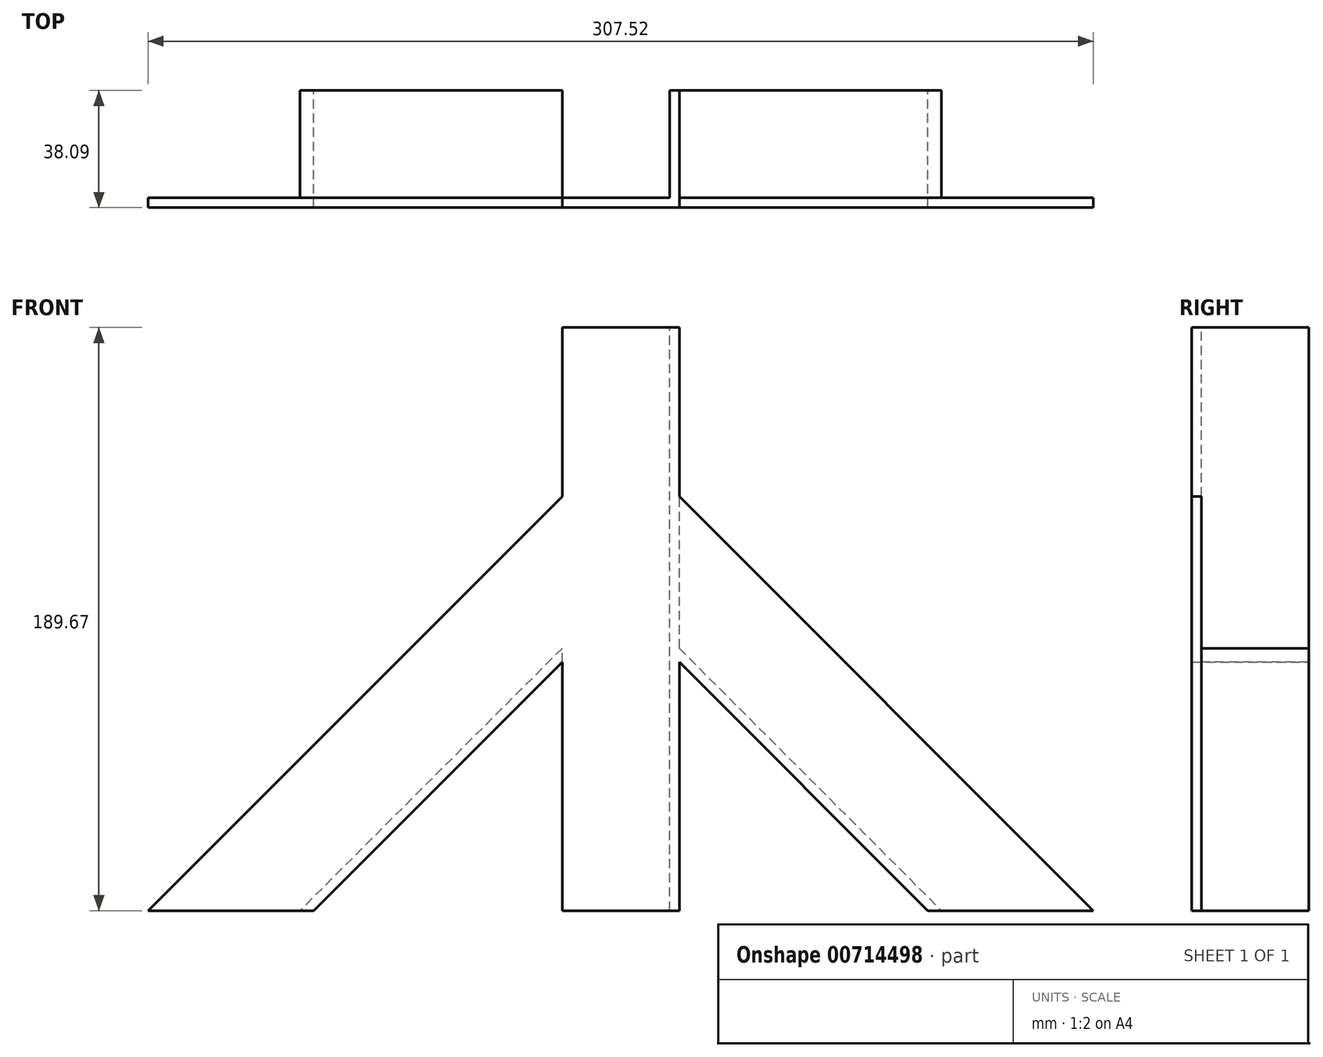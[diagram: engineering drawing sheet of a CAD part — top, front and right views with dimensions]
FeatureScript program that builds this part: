
annotation { "Feature Type Name" : "Feature", "Feature Type Description" : "" }
export const myFeature = defineFeature(function(context is Context, id is Id, definition is map)
    precondition{}
    {
        {
            var Q0;
            Q0=qCreatedBy(makeId("Front.planeOp"),FACE);
            var sketch = newSketch(context, id + "F0", { "sketchPlane" : qUnion([Q0])});
            skLineSegment(sketch, "E0.bottom", {"start": v(0, 0) * mm, "end": v(38.1, 0) * mm});
            skLineSegment(sketch, "E0.top", {"start": v(0, 189.67) * mm, "end": v(38.1, 189.67) * mm});
            skLineSegment(sketch, "E0.left", {"start": v(0, 0) * mm, "end": v(0, 189.67) * mm});
            skLineSegment(sketch, "E0.right", {"start": v(38.1, 0) * mm, "end": v(38.1, 189.67) * mm});
            skLineSegment(sketch, "E1", {"start": v(-80.83, 0) * mm, "end": v(0, 80.83) * mm});
            skLineSegment(sketch, "E2", {"start": v(-134.7, 0) * mm, "end": v(0, 134.7) * mm});
            skLineSegment(sketch, "E3", {"start": v(38.1, 134.7) * mm, "end": v(172.8, 0) * mm});
            skLineSegment(sketch, "E4", {"start": v(118.93, 0) * mm, "end": v(38.1, 80.83) * mm});
            skLineSegment(sketch, "E5", {"start": v(-134.7, 0) * mm, "end": v(-80.83, 0) * mm});
            skLineSegment(sketch, "E6", {"start": v(118.93, 0) * mm, "end": v(172.8, 0) * mm});
            skSolve(sketch);
        }
        {
            var Q0;
            {var subQ3=sQuery(id+"F0.wireOp",EDGE,"E0.bottom");Q0=makeQuery(id+"F0.imprint","IMPRINT",FACE,{"disambiguationData":[TD([[makeQuery(id+"F0.imprint","IMPRINT",EDGE,{"derivedFrom":subQ3}),1.0]])]});}
            var Q1;
            {var subQ0=sQuery(id+"F0.wireOp",EDGE,"E1");Q1=makeQuery(id+"F0.imprint","IMPRINT",FACE,{"disambiguationData":[TD([[makeQuery(id+"F0.imprint","IMPRINT",EDGE,{"derivedFrom":subQ0}),1.0]])]});}
            var Q2;
            {var subQ0=sQuery(id+"F0.wireOp",EDGE,"E3");Q2=makeQuery(id+"F0.imprint","IMPRINT",FACE,{"disambiguationData":[TD([[makeQuery(id+"F0.imprint","IMPRINT",EDGE,{"derivedFrom":subQ0}),-1.0]])]});}
            extrude(context, id + "F1", {"entities" : qUnion([Q0, Q1, Q2]), "depth" : 3.17 * mm, "offsetDistance" : 25.4 * mm});
        }
        {
            var Q0;
            Q0=makeQuery(id+"F1.opExtrude","CAP_FACE",FACE,{"disambiguationData":[OSD([sQuery(id+"F0.wireOp",EDGE,"E0.bottom"),sQuery(id+"F0.wireOp",EDGE,"E0.top"),sQuery(id+"F0.wireOp",EDGE,"E0.left"),sQuery(id+"F0.wireOp",EDGE,"E0.right"),sQuery(id+"F0.wireOp",EDGE,"E1"),sQuery(id+"F0.wireOp",EDGE,"E2"),sQuery(id+"F0.wireOp",EDGE,"E3"),sQuery(id+"F0.wireOp",EDGE,"E4"),sQuery(id+"F0.wireOp",EDGE,"E5"),sQuery(id+"F0.wireOp",EDGE,"E6")])],"isStart":true});
            var sketch = newSketch(context, id + "F2", { "sketchPlane" : qUnion([Q0])});
            skLineSegment(sketch, "E7.bottom", {"start": v(-38.1, 0) * mm, "end": v(-34.92, 0) * mm});
            skLineSegment(sketch, "E7.top", {"start": v(-38.1, 189.67) * mm, "end": v(-34.93, 189.67) * mm});
            skLineSegment(sketch, "E7.left", {"start": v(-38.1, 0) * mm, "end": v(-38.1, 189.67) * mm});
            skLineSegment(sketch, "E7.right", {"start": v(-34.92, 0) * mm, "end": v(-34.93, 189.67) * mm});
            skSolve(sketch);
        }
        {
            var Q0;
            {var subQ3=sQuery(id+"F2.wireOp",EDGE,"E7.bottom");Q0=makeQuery(id+"F2.imprint","IMPRINT",FACE,{"disambiguationData":[TD([[makeQuery(id+"F2.imprint","IMPRINT",EDGE,{"derivedFrom":subQ3}),-1.0]])]});}
            extrude(context, id + "F3", {"entities" : qUnion([Q0]), "operationType" : NewBodyOperationType.ADD, "depth" : 34.92 * mm, "offsetDistance" : 25.4 * mm});
        }
        {
            var Q0;
            {var subQ0=sQuery(id+"F0.wireOp",EDGE,"E3");var subQ1=sQuery(id+"F0.wireOp",EDGE,"E0.right");var subQ2=sQuery(id+"F0.wireOp",EDGE,"E0.top");var subQ3=sQuery(id+"F0.wireOp",EDGE,"E4");var subQ4=sQuery(id+"F0.wireOp",EDGE,"E0.bottom");var subQ5=sQuery(id+"F0.wireOp",EDGE,"E6");Q0=makeQuery(id+"F3.boolean.opBoolean","SPLIT",FACE,{"disambiguationData":[TD([makeQuery(id+"F1.opExtrude","SWEPT_FACE",FACE,{"disambiguationData":[OSD([subQ0])]})])],"derivedFrom":makeQuery(id+"F1.opExtrude","CAP_FACE",FACE,{"disambiguationData":[OSD([subQ4,subQ2,sQuery(id+"F0.wireOp",EDGE,"E0.left"),subQ1,sQuery(id+"F0.wireOp",EDGE,"E1"),sQuery(id+"F0.wireOp",EDGE,"E2"),subQ0,subQ3,sQuery(id+"F0.wireOp",EDGE,"E5"),subQ5])],"isStart":true})});}
            var sketch = newSketch(context, id + "F4", { "sketchPlane" : qUnion([Q0])});
            skLineSegment(sketch, "E8", {"start": v(-118.93, 0) * mm, "end": v(-38.1, 80.83) * mm});
            skLineSegment(sketch, "E9", {"start": v(-38.1, 80.83) * mm, "end": v(-38.1, 85.32) * mm});
            skLineSegment(sketch, "E10", {"start": v(-38.1, 85.32) * mm, "end": v(-123.42, 0) * mm});
            skLineSegment(sketch, "E11", {"start": v(-123.42, 0) * mm, "end": v(-118.93, 0) * mm});
            skSolve(sketch);
        }
        {
            var Q0;
            Q0=makeQuery(id+"F4.imprint","IMPRINT",FACE,{"disambiguationData":[TD([[makeQuery(id+"F4.imprint","IMPRINT",EDGE,{"derivedFrom":sQuery(id+"F4.wireOp",EDGE,"E8")}),1.0]])]});
            extrude(context, id + "F5", {"entities" : qUnion([Q0]), "operationType" : NewBodyOperationType.ADD, "depth" : 34.92 * mm, "offsetDistance" : 25.4 * mm});
        }
        {
            var Q0;
            {var subQ0=sQuery(id+"F0.wireOp",EDGE,"E0.left");var subQ1=sQuery(id+"F0.wireOp",EDGE,"E0.bottom");var subQ2=sQuery(id+"F0.wireOp",EDGE,"E1");var subQ3=sQuery(id+"F0.wireOp",EDGE,"E0.top");var subQ4=sQuery(id+"F0.wireOp",EDGE,"E2");var subQ5=sQuery(id+"F0.wireOp",EDGE,"E5");Q0=makeQuery(id+"F3.boolean.opBoolean","SPLIT",FACE,{"disambiguationData":[TD([makeQuery(id+"F1.opExtrude","SWEPT_FACE",FACE,{"disambiguationData":[OSD([subQ1])]})])],"derivedFrom":makeQuery(id+"F1.opExtrude","CAP_FACE",FACE,{"disambiguationData":[OSD([subQ1,subQ3,subQ0,sQuery(id+"F0.wireOp",EDGE,"E0.right"),subQ2,subQ4,sQuery(id+"F0.wireOp",EDGE,"E3"),sQuery(id+"F0.wireOp",EDGE,"E4"),subQ5,sQuery(id+"F0.wireOp",EDGE,"E6")])],"isStart":true})});}
            var sketch = newSketch(context, id + "F6", { "sketchPlane" : qUnion([Q0])});
            skLineSegment(sketch, "E12", {"start": v(80.83, 0) * mm, "end": v(0, 80.83) * mm});
            skLineSegment(sketch, "E13", {"start": v(0, 80.83) * mm, "end": v(0, 85.32) * mm});
            skLineSegment(sketch, "E14", {"start": v(0, 85.32) * mm, "end": v(85.32, 0) * mm});
            skLineSegment(sketch, "E15", {"start": v(85.32, 0) * mm, "end": v(80.83, 0) * mm});
            skSolve(sketch);
        }
        {
            var Q0;
            Q0=makeQuery(id+"F6.imprint","IMPRINT",FACE,{"disambiguationData":[TD([[makeQuery(id+"F6.imprint","IMPRINT",EDGE,{"derivedFrom":sQuery(id+"F6.wireOp",EDGE,"E12")}),-1.0]])]});
            extrude(context, id + "F7", {"entities" : qUnion([Q0]), "operationType" : NewBodyOperationType.ADD, "depth" : 34.92 * mm, "offsetDistance" : 25.4 * mm});
        }
    });
